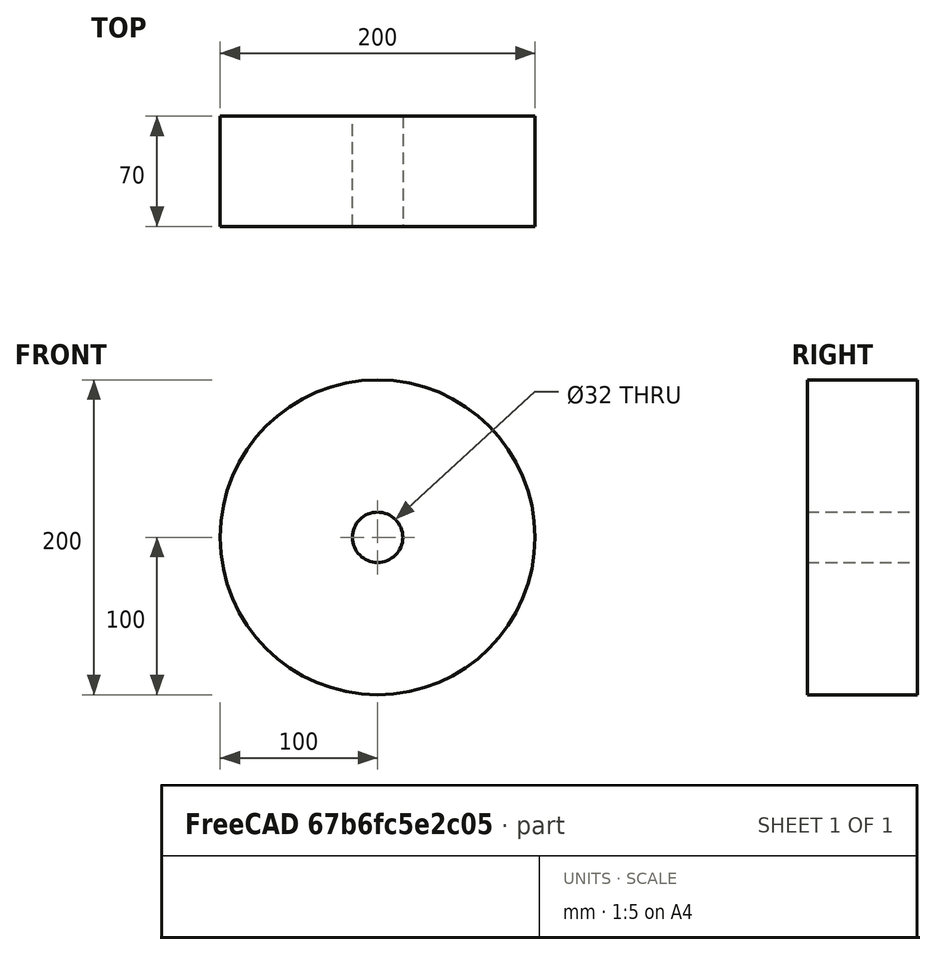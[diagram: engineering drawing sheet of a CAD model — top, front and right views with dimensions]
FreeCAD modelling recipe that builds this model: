
FCSTD DOCUMENT  (FreeCAD 0.18R14555 (Git shallow))
Label: filament
License: All rights reserved
LicenseURL: http://en.wikipedia.org/wiki/All_rights_reserved
objects: Sketcher::SketchObject×1, PartDesign::Pad×1, PartDesign::Body×1
note: 4 computed .brp shape members not serialized (recipe doc carries the construction recipe); baked Part::Feature solids carry a one-line shape summary decoded from their .brp

FEATURE [Sketcher::SketchObject] Sketch
  MapMode = 5
  Placement = pos=(0,0,0) rot=(1,0,0;1.5708rad)
  Support = -> [XZ_Plane]
  sketch-geometry (2):
    g0: Circle CenterX=0 CenterY=0 CenterZ=0 NormalX=0 NormalY=0 NormalZ=1 AngleXU=0 Radius=16
    g1: Circle CenterX=0 CenterY=0 CenterZ=0 NormalX=0 NormalY=0 NormalZ=1 AngleXU=0 Radius=100
  constraints (4):
    c: Coincident(g0,g-1)
    c: Coincident(g1,g0)
    c: Radius(g0) = 16
    c: Radius(g1) = 100
FEATURE [PartDesign::Pad] Pad
  Length = 70
  Length2 = 100
  Placement = pos=(0,0,0) rot=(1,0,0;1.5708rad)
  Profile = -> Sketch
  Type = 0
FEATURE [PartDesign::Body] Body
  Group = -> [Sketch,Pad]
  Origin = -> Origin
  Tip = -> Pad
